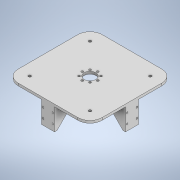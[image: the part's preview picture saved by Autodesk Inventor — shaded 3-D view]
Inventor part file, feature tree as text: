
AUTODESK INVENTOR PART (.ipt)
format: ipt  version: 2021 (Build 250183000, 183)  size: 251,904 bytes
history: native  units: mm
features: sketch x9, projected_geometry x7, hole x6, extrude x3, other x1, pattern_circular x1, fillet x1, chamfer x1, mirror x1
ambient origin geometry x8: Origin, YZ Plane, XZ Plane, XY Plane, X Axis, Y Axis, Z Axis, Center Point
bodies: Body1 (feature_tree)
feature tree (30):
  other  "實體1"
  extrude  "擠出1"  Depth=174.0mm
  extrude  "擠出2"  Depth=174.0mm
  hole  "孔1"  [1 undecoded]
  pattern_circular  "環形陣列1"  [2 undecoded]
  fillet  "圓角1"  [1 undecoded]
  extrude  "擠出3"  Depth=16.0mm
  chamfer  "倒角1"  Distance=80.0mm Angle=360.0deg
  hole  "孔2"  [1 undecoded]
  hole  "孔3"  [1 undecoded]
  mirror  "鏡射1"
  hole  "孔4"  [1 undecoded]
  hole  "孔5"  [1 undecoded]
  hole  "孔6"  [1 undecoded]
  sketch  "草圖1"
  sketch  "草圖2"
  sketch  "草圖3"
  sketch  "草圖4"
  projected_geometry  "投影迴路1"
  sketch  "草圖6"
  projected_geometry  "投影迴路2"
  sketch  "草圖7"
  sketch  "草圖8"
  projected_geometry  "投影迴路3"
  sketch  "草圖9"
  projected_geometry  "投影迴路4"
  projected_geometry  "投影迴路5"
  projected_geometry  "投影迴路6"
  projected_geometry  "投影迴路7"
  sketch  "草圖10"
note: 9 required parameter values undecoded (feature->parameter linkage not recoverable at this tier; creation-order binding heuristic only, values carry confidence <= 0.55)
